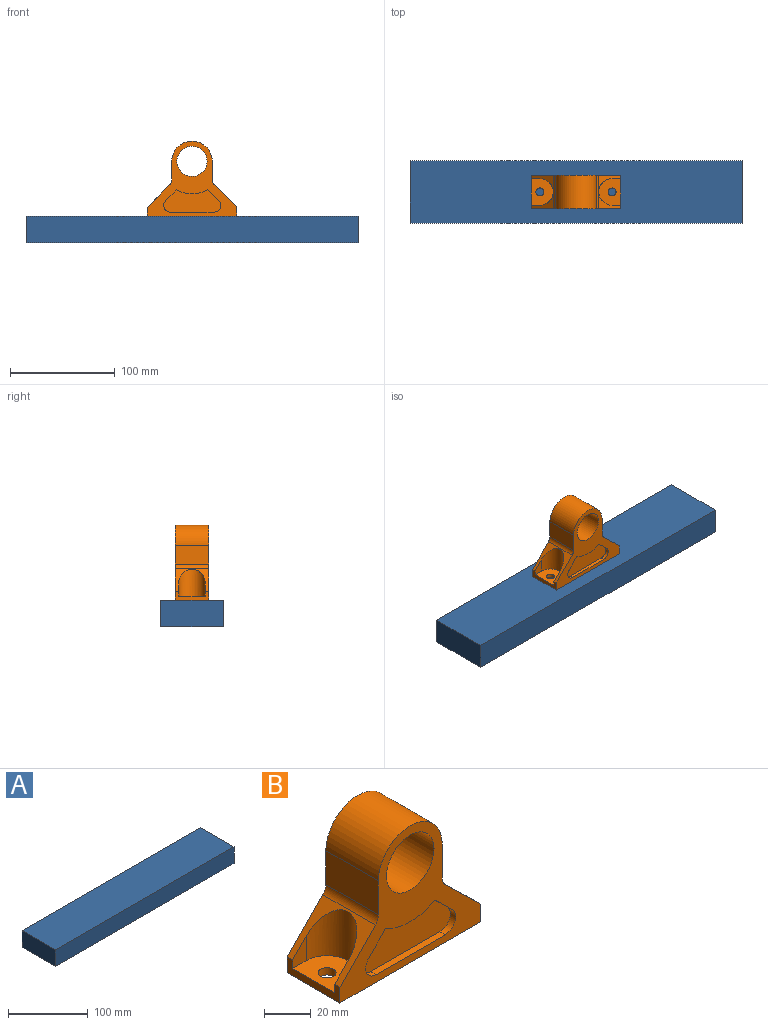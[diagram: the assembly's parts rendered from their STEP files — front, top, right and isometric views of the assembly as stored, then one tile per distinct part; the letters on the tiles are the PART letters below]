
ASSEMBLY  parts=2 mates=1
PART A: 6 faces, bbox 316.5x59.2x25.4 mm
  f0: plane 59.24x25.4mm, normal (-1,0,0), area 1504.6mm2, adj f1,f3,f4,f5
  f1: plane 316.49x25.4mm, normal (0,-1,0), area 8038.8mm2, adj f0,f2,f4,f5
  f2: plane 59.24x25.4mm, normal (1,0,0), area 1504.6mm2, adj f1,f3,f4,f5
  f3: plane 316.49x25.4mm, normal (0,1,0), area 8038.8mm2, adj f0,f2,f4,f5
  f4: plane 316.49x59.24mm, normal (0,0,1), area 18747.9mm2, adj f0,f1,f2,f3
  f5: plane 316.49x59.24mm, normal (0,0,-1), area 18747.9mm2, adj f0,f1,f2,f3
PART B: 37 faces, bbox 85x31.8x71.6 mm
  f0: plane 31.75x21.33mm, normal (0.7,0,0.72), area 303.9mm2, adj f2,f4,f5,f12,f32,f33,f34
  f1: plane 31.75x8.27mm, normal (-1,0,0), area 149mm2, adj f2,f3,f11,f12,f27,f28,f30
  f2: plane 85.01x71.57mm, normal (0,-1,0), area 1991.1mm2, adj f0,f1,f3,f4,f5,f6,f7,f8
  f3: plane 85.01x31.75mm, normal (0,0,-1), area 2607.9mm2, adj f1,f2,f4,f12,f31,f36
  f4: plane 31.75x9.28mm, normal (1,0,0), area 155.3mm2, adj f0,f2,f3,f12,f32,f34,f35
  f5: cylinder r=6.35mm len=31.75mm, axis (0,1,0), area 161mm2, adj f0,f2,f6,f12
  f6: plane 31.75x17.71mm, normal (1,0,0), area 562.3mm2, adj f2,f5,f7,f12
  f7: cylinder r=19.26mm len=38.51mm, axis (0,1,0), area 1920.8mm2, adj f2,f6,f8,f12
  f8: plane 31.75x17.79mm, normal (-1,0,0), area 564.9mm2, adj f2,f7,f9,f12
  f9: cylinder r=6.35mm len=31.75mm, axis (0,1,0), area 156.6mm2, adj f2,f8,f11,f12
  f10: cylinder r=14.35mm len=31.75mm, axis (0,1,0), area 2862.8mm2, adj f2,f12
  f11: plane 31.75x21.79mm, normal (-0.71,0,0.7), area 315mm2, adj f1,f2,f9,f12,f27,f28,f29
  f12: plane 85.01x71.57mm, normal (0,1,0), area 1991.1mm2, adj f0,f1,f3,f4,f5,f6,f7,f8
  f13: cylinder r=31.03mm len=29.89mm, axis (0,-1,0), area 99mm2, adj f2,f14,f18,f19
  f14: plane 10.39x10.21mm, normal (0.71,0,-0.7), area 46.3mm2, adj f2,f13,f15,f19
  f15: cylinder r=6.35mm len=10.8mm, axis (0,-1,0), area 47.3mm2, adj f2,f14,f16,f19
  f16: plane 41.71x3.18mm, normal (0,0,1), area 132.4mm2, adj f2,f15,f17,f19
  f17: cylinder r=6.35mm len=10.9mm, axis (0,-1,0), area 47.8mm2, adj f2,f16,f18,f19
  f18: plane 10.57x10.29mm, normal (-0.7,0,-0.72), area 46.8mm2, adj f2,f13,f17,f19
  f19: plane 54.41x21.19mm, normal (0,-1,0), area 907mm2, adj f13,f14,f15,f16,f17,f18
  f20: cylinder r=31.03mm len=29.89mm, axis (0,1,0), area 99mm2, adj f12,f21,f25,f26
  f21: plane 10.57x10.29mm, normal (-0.7,0,-0.72), area 46.8mm2, adj f12,f20,f22,f26
  f22: cylinder r=6.35mm len=10.9mm, axis (0,1,0), area 47.8mm2, adj f12,f21,f23,f26
  f23: plane 41.71x3.18mm, normal (0,0,1), area 132.4mm2, adj f12,f22,f24,f26
  f24: cylinder r=6.35mm len=10.8mm, axis (0,1,0), area 47.3mm2, adj f12,f23,f25,f26
  f25: plane 10.39x10.21mm, normal (0.71,0,-0.7), area 46.3mm2, adj f12,f20,f24,f26
  f26: plane 54.41x21.19mm, normal (0,1,0), area 907mm2, adj f20,f21,f22,f23,f24,f25
  f27: plane 12.73x8.12mm, normal (0,-1,0), area 69.8mm2, adj f1,f11,f29,f30
  f28: plane 12.73x8.12mm, normal (0,1,0), area 69.8mm2, adj f1,f11,f29,f30
  f29: cylinder r=12.7mm len=25.69mm, axis (0,0,1), area 836.1mm2, adj f11,f27,f28,f30
  f30: plane 25.4x20.82mm, normal (0,0,1), area 413.9mm2, adj f1,f27,f28,f29,f31
  f31: cylinder r=3.81mm len=7.62mm, axis (0,0,1), area 90.9mm2, adj f3,f30
  f32: plane 13.39x8.12mm, normal (0,-1,0), area 76.6mm2, adj f0,f4,f33,f35
  f33: cylinder r=12.7mm len=25.8mm, axis (0,0,1), area 848.2mm2, adj f0,f32,f34,f35
  f34: plane 13.39x8.12mm, normal (0,1,0), area 76.6mm2, adj f0,f4,f33,f35
  f35: plane 25.4x20.82mm, normal (0,0,1), area 413.9mm2, adj f4,f32,f33,f34,f36
  f36: cylinder r=3.81mm len=7.62mm, axis (0,0,1), area 90.9mm2, adj f3,f35
PLACE A t=(16.27,-73.89,-77.71)mm
PLACE B at identity
MATE fastened A.f4 <-> B.f3  axis (0,0,1) through (0,0,-52.31)mm
